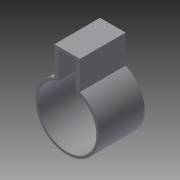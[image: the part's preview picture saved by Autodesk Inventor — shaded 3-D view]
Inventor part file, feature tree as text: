
AUTODESK INVENTOR PART (.ipt)
format: ipt  version: 2015 (Build 190159000, 159)  size: 178,176 bytes
history: native  units: in
note: dims shown in document units (in); Inventor stores cm internally (conversion verified against a paired STEP export)
features: reference x4, extrude x3, sketch x3, plane x1
ambient origin geometry x8: Origin, YZ Plane, XZ Plane, XY Plane, X Axis, Y Axis, Z Axis, Center Point
bodies: Solid1 (feature_tree)
feature tree (11):
  plane  "Work Plane1"
  extrude  "Extrusion1"  Depth=0.1969in
  extrude  "Extrusion2"  Depth=0.1181in
  extrude  "Extrusion4"  Depth=1.9685in TaperAngle=0.0deg
  sketch  "Sketch1"  dims[d0=0.409in d2=0.1969in d3=0.1969in d5=0.3937in]
  reference  "Reference6"
  reference  "Reference7"
  reference  "Reference8"
  reference  "Reference9"
  sketch  "Sketch2"  dims[d6=0.1969in d7=0.0in d8=0.1181in]
  sketch  "Sketch3"  dims[d9=0.1181in d10=1.9685in d11=0.0in d14=0.7874in d15=0.3937in d16=0.0787in d18=0.3937in d19=0.0787in d20=0.1969in d21=0.0in]
